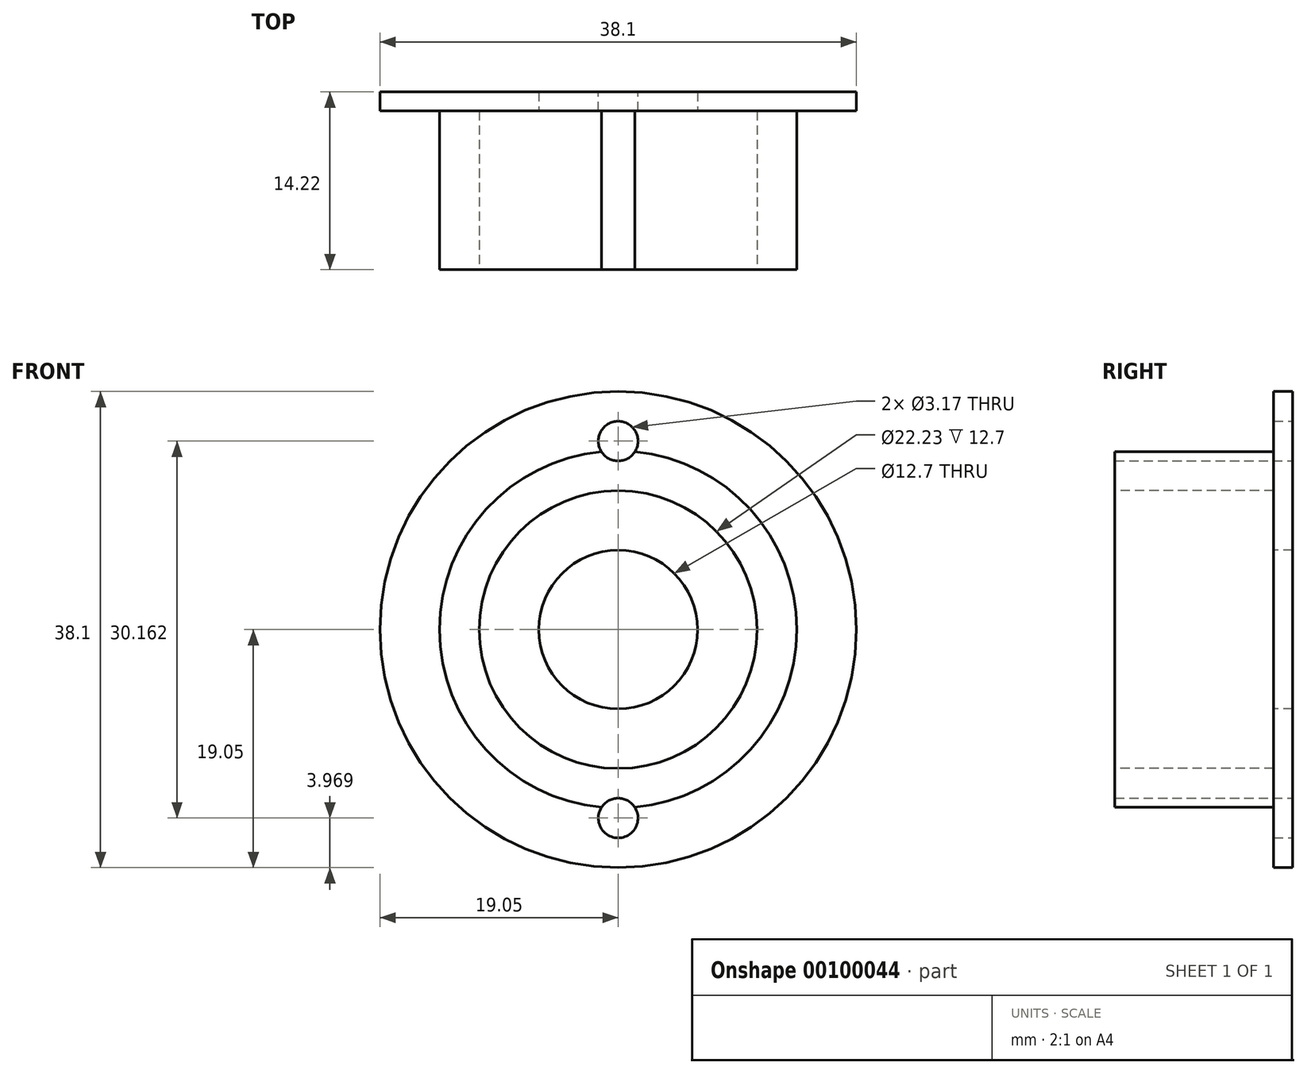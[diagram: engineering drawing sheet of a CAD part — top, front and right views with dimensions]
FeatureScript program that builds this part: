
annotation { "Feature Type Name" : "Feature", "Feature Type Description" : "" }
export const myFeature = defineFeature(function(context is Context, id is Id, definition is map)
    precondition{}
    {
        {
            var Q0;
            Q0=qCreatedBy(makeId("Front.planeOp"),FACE);
            var sketch = newSketch(context, id + "F0", { "sketchPlane" : qUnion([Q0])});
            skCircle(sketch, "E0", {"center": v(0, 0) * mm, "radius": 11.11 * mm});
            skCircle(sketch, "E1", {"center": v(0, 0) * mm, "radius": 14.29 * mm});
            skSolve(sketch);
        }
        {
            var Q0;
            Q0 = qSketchRegion(id + "F0", true);
            extrude(context, id + "F1", {"entities" : qUnion([Q0]), "oppositeDirection" : true, "depth" : 12.7 * mm});
        }
        {
            var Q0;
            Q0=makeQuery(id+"F1.opExtrude","CAP_FACE",FACE,{"disambiguationData":[OSD([sQuery(id+"F0.wireOp",EDGE,"E0"),sQuery(id+"F0.wireOp",EDGE,"E1")])],"isStart":false});
            var sketch = newSketch(context, id + "F2", { "sketchPlane" : qUnion([Q0])});
            skCircle(sketch, "E2", {"center": v(0, 0) * mm, "radius": 19.05 * mm});
            skCircle(sketch, "E3", {"center": v(0, 0) * mm, "radius": 6.35 * mm});
            skCircle(sketch, "E4", {"center": v(0, 15.08) * mm, "radius": 1.59 * mm});
            skCircle(sketch, "E5", {"center": v(0, -15.08) * mm, "radius": 1.59 * mm});
            skLineSegment(sketch, "E6", {"start": v(0, 15.08) * mm, "end": v(0, 0) * mm, "construction": true});
            skLineSegment(sketch, "E7", {"start": v(0, 0) * mm, "end": v(0, -15.08) * mm, "construction": true});
            skSolve(sketch);
        }
        {
            var Q0;
            Q0 = qSketchRegion(id + "F2", true);
            var Q1;
            {var subQ0=sQuery(id+"F2.wireOp",EDGE,"E4");var subQ1=makeQuery(id+"F1.opExtrude","CAP_EDGE",EDGE,{"disambiguationData":[OSD([sQuery(id+"F0.wireOp",EDGE,"E1")])],"isStart":false});var subQ2=makeQuery(id+"F2.imprint","INTERSECT",VERTEX,{"disambiguationData":[OD(0.0)],"derivedFrom":[subQ1,subQ0]});Q1=makeQuery(id+"F2.imprint","IMPRINT",FACE,{"disambiguationData":[TD([[makeQuery(id+"F2.imprint","IMPRINT",EDGE,{"disambiguationData":[TD([[subQ2,-1.0]])],"derivedFrom":subQ0}),1.0]])]});}
            var Q2;
            {var subQ0=sQuery(id+"F2.wireOp",EDGE,"E5");var subQ1=makeQuery(id+"F1.opExtrude","CAP_EDGE",EDGE,{"disambiguationData":[OSD([sQuery(id+"F0.wireOp",EDGE,"E1")])],"isStart":false});var subQ2=makeQuery(id+"F2.imprint","INTERSECT",VERTEX,{"disambiguationData":[OD(0.0)],"derivedFrom":[subQ1,subQ0]});Q2=makeQuery(id+"F2.imprint","IMPRINT",FACE,{"disambiguationData":[TD([[makeQuery(id+"F2.imprint","IMPRINT",EDGE,{"disambiguationData":[TD([[subQ2,1.0]])],"derivedFrom":subQ0}),1.0]])]});}
            var Q3;
            {var subQ0=sQuery(id+"F2.wireOp",EDGE,"E5");var subQ1=makeQuery(id+"F1.opExtrude","CAP_EDGE",EDGE,{"disambiguationData":[OSD([sQuery(id+"F0.wireOp",EDGE,"E1")])],"isStart":false});var subQ2=makeQuery(id+"F2.imprint","INTERSECT",VERTEX,{"disambiguationData":[OD(0.0)],"derivedFrom":[subQ1,subQ0]});Q3=makeQuery(id+"F2.imprint","IMPRINT",FACE,{"disambiguationData":[TD([[makeQuery(id+"F2.imprint","IMPRINT",EDGE,{"disambiguationData":[TD([[subQ2,-1.0]])],"derivedFrom":subQ0}),1.0]])]});}
            var Q4;
            {var subQ0=sQuery(id+"F2.wireOp",EDGE,"E4");var subQ1=makeQuery(id+"F1.opExtrude","CAP_EDGE",EDGE,{"disambiguationData":[OSD([sQuery(id+"F0.wireOp",EDGE,"E1")])],"isStart":false});var subQ2=makeQuery(id+"F2.imprint","INTERSECT",VERTEX,{"disambiguationData":[OD(0.0)],"derivedFrom":[subQ1,subQ0]});Q4=makeQuery(id+"F2.imprint","IMPRINT",FACE,{"disambiguationData":[TD([[makeQuery(id+"F2.imprint","IMPRINT",EDGE,{"disambiguationData":[TD([[subQ2,1.0]])],"derivedFrom":subQ0}),1.0]])]});}
            extrude(context, id + "F3", {"entities" : qUnion([Q0, Q1, Q2, Q3, Q4]), "operationType" : NewBodyOperationType.ADD, "depth" : 1.52 * mm});
        }
        {
            var Q0;
            Q0=makeQuery(id+"F3.opExtrude","CAP_FACE",FACE,{"disambiguationData":[OSD([sQuery(id+"F2.wireOp",EDGE,"E2"),sQuery(id+"F2.wireOp",EDGE,"E3")])],"isStart":false});
            var sketch = newSketch(context, id + "F4", { "sketchPlane" : qUnion([Q0])});
            skCircle(sketch, "E8.0", {"center": v(0, 15.08) * mm, "radius": 1.59 * mm});
            skCircle(sketch, "E8.1", {"center": v(0, -15.08) * mm, "radius": 1.59 * mm});
            skSolve(sketch);
        }
        {
            var Q0;
            Q0 = qSketchRegion(id + "F4", true);
            extrude(context, id + "F5", {"entities" : qUnion([Q0]), "operationType" : NewBodyOperationType.REMOVE, "oppositeDirection" : true, "depth" : 25.4 * mm});
        }
    });
